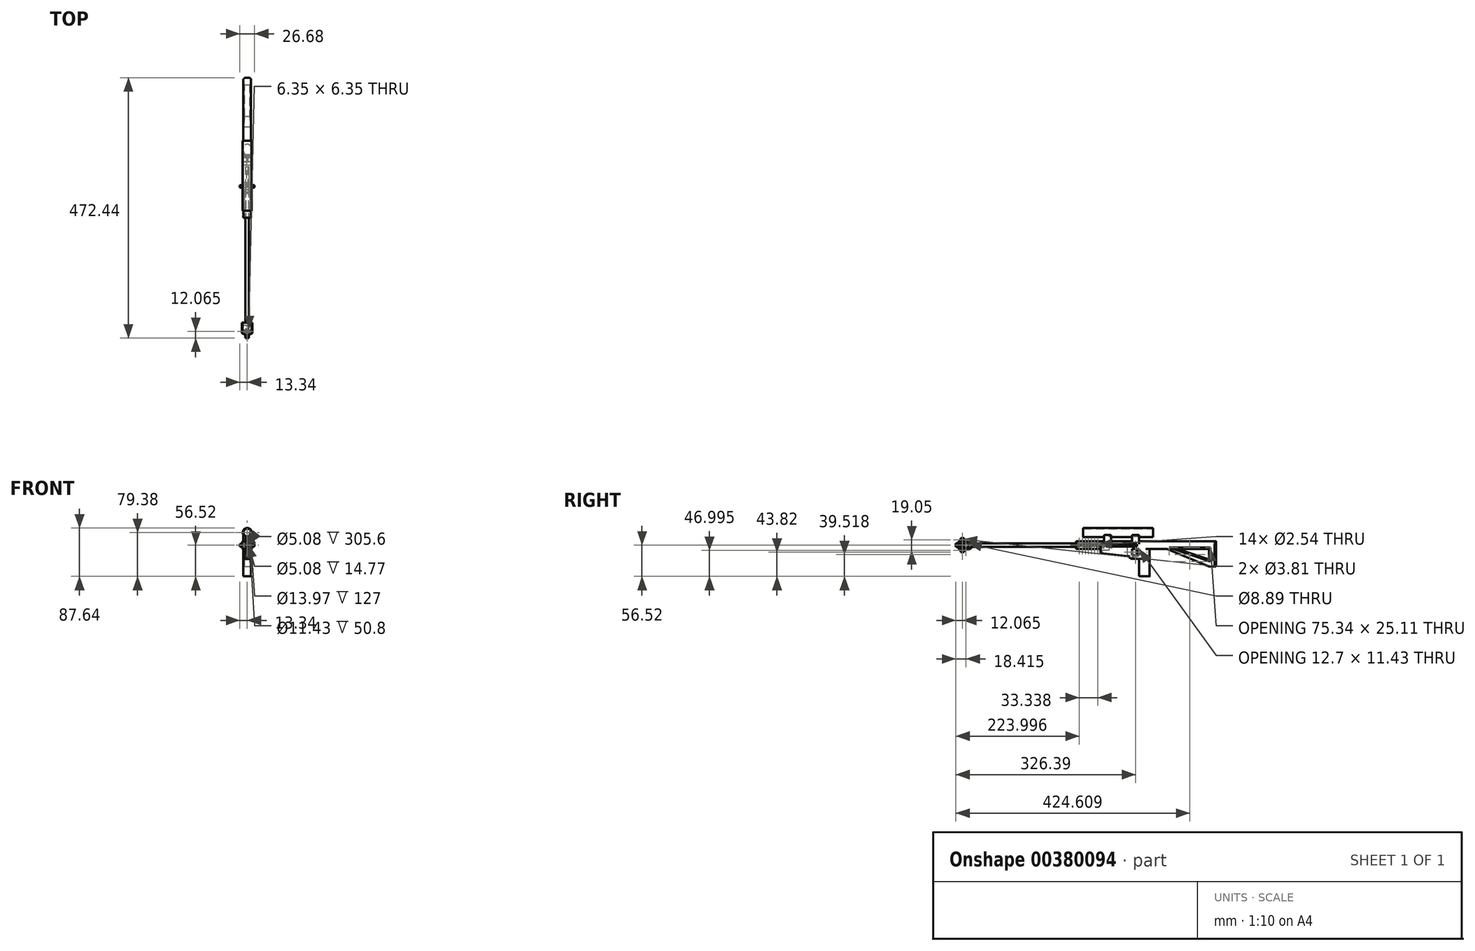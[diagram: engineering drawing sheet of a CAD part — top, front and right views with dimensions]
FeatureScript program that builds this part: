
annotation { "Feature Type Name" : "Feature", "Feature Type Description" : "" }
export const myFeature = defineFeature(function(context is Context, id is Id, definition is map)
    precondition{}
    {
        {
            var Q0;
            Q0=qCreatedBy(makeId("Front.planeOp"),FACE);
            var sketch = newSketch(context, id + "F0", { "sketchPlane" : qUnion([Q0])});
            skLineSegment(sketch, "E0.bottom", {"start": v(9.53, -6.35) * mm, "end": v(-9.53, -6.35) * mm});
            skLineSegment(sketch, "E0.top", {"start": v(9.53, 6.35) * mm, "end": v(-9.53, 6.35) * mm});
            skLineSegment(sketch, "E0.left", {"start": v(9.53, -6.35) * mm, "end": v(9.53, 6.35) * mm});
            skLineSegment(sketch, "E0.right", {"start": v(-9.53, -6.35) * mm, "end": v(-9.53, 6.35) * mm});
            skPoint(sketch, "E0.middle", {"position": v(0, 0) * mm});
            skSolve(sketch);
        }
        {
            var Q0;
            Q0=qSketchRegion(id+"F0",true);
            extrude(context, id + "F1", {"entities" : qUnion([Q0]), "depth" : 25.4 * mm});
        }
        {
            var Q0;
            Q0=makeQuery(id+"F1.opExtrude","CAP_FACE",FACE,{"disambiguationData":[OSD([sQuery(id+"F0.wireOp",EDGE,"E0.bottom"),sQuery(id+"F0.wireOp",EDGE,"E0.top"),sQuery(id+"F0.wireOp",EDGE,"E0.left"),sQuery(id+"F0.wireOp",EDGE,"E0.right")])],"isStart":true});
            var sketch = newSketch(context, id + "F2", { "sketchPlane" : qUnion([Q0])});
            skCircle(sketch, "E1", {"center": v(0, 0) * mm, "radius": 3.18 * mm});
            skSolve(sketch);
        }
        {
            var Q0;
            Q0=qSketchRegion(id+"F2",true);
            extrude(context, id + "F3", {"entities" : qUnion([Q0]), "operationType" : NewBodyOperationType.ADD, "depth" : 190.5 * mm});
        }
        {
            var Q0;
            Q0=qCreatedBy(makeId("Front.planeOp"),FACE);
            var sketch = newSketch(context, id + "F4", { "sketchPlane" : qUnion([Q0])});
            skLineSegment(sketch, "E2.bottom", {"start": v(3.17, -12.7) * mm, "end": v(-3.18, -12.7) * mm});
            skLineSegment(sketch, "E2.top", {"start": v(3.18, 12.7) * mm, "end": v(-3.17, 12.7) * mm});
            skLineSegment(sketch, "E2.left", {"start": v(3.17, -12.7) * mm, "end": v(3.18, 12.7) * mm});
            skLineSegment(sketch, "E2.right", {"start": v(-3.18, -12.7) * mm, "end": v(-3.17, 12.7) * mm});
            skPoint(sketch, "E2.middle", {"position": v(0, 0) * mm});
            skSolve(sketch);
        }
        {
            var Q0;
            Q0 = qSketchRegion(id + "F4", true);
            extrude(context, id + "F5", {"entities" : qUnion([Q0]), "operationType" : NewBodyOperationType.ADD, "depth" : 19.05 * mm, "hasSecondDirection" : true, "secondDirectionOppositeDirection" : true, "secondDirectionDepth" : -12.7 * mm});
        }
        {
            var Q0;
            Q0=makeQuery(id+"F3.opExtrude","CAP_FACE",FACE,{"disambiguationData":[OSD([sQuery(id+"F2.wireOp",EDGE,"E1")])],"isStart":false});
            var sketch = newSketch(context, id + "F6", { "sketchPlane" : qUnion([Q0])});
            skLineSegment(sketch, "E3.bottom", {"start": v(6.99, -6.99) * mm, "end": v(-6.99, -6.99) * mm});
            skLineSegment(sketch, "E3.top", {"start": v(6.98, 6.99) * mm, "end": v(-6.98, 6.99) * mm});
            skLineSegment(sketch, "E3.left", {"start": v(6.99, -6.99) * mm, "end": v(6.99, 6.98) * mm});
            skLineSegment(sketch, "E3.right", {"start": v(-6.99, -6.99) * mm, "end": v(-6.99, 6.98) * mm});
            skPoint(sketch, "E3.middle", {"position": v(0, 0) * mm});
            skSolve(sketch);
        }
        {
            var Q0;
            Q0=qSketchRegion(id+"F6",true);
            extrude(context, id + "F7", {"entities" : qUnion([Q0]), "operationType" : NewBodyOperationType.ADD, "depth" : 254 * mm});
        }
        {
            var Q0;
            Q0=makeQuery(id+"F7.opExtrude","SWEPT_FACE",FACE,{"disambiguationData":[OSD([sQuery(id+"F6.wireOp",EDGE,"E3.right")])]});
            var sketch = newSketch(context, id + "F8", { "sketchPlane" : qUnion([Q0])});
            skLineSegment(sketch, "E4", {"start": v(444.5, -6.99) * mm, "end": v(444.5, -38.74) * mm});
            skLineSegment(sketch, "E5", {"start": v(444.5, -38.74) * mm, "end": v(431.8, -38.74) * mm});
            skLineSegment(sketch, "E6", {"start": v(431.8, -38.74) * mm, "end": v(431.8, -6.99) * mm});
            skSolve(sketch);
        }
        {
            var Q0;
            Q0=qSketchRegion(id+"F8",true);
            var Q1;
            {var subQ0=sQuery(id+"F8.wireOp",EDGE,"E4");Q1=makeQuery(id+"F8.imprint","IMPRINT",FACE,{"disambiguationData":[TD([[makeQuery(id+"F8.imprint","IMPRINT",EDGE,{"derivedFrom":subQ0}),-1.0]])]});}
            extrude(context, id + "F9", {"entities" : qUnion([Q0, Q1]), "operationType" : NewBodyOperationType.ADD, "depth" : -13.97 * mm});
        }
        {
            var Q0;
            {var subQ0=sQuery(id+"F6.wireOp",EDGE,"E3.right");Q0=makeQuery(id+"F9.boolean.opBoolean","MERGE",FACE,{"derivedFrom":[makeQuery(id+"F7.opExtrude","SWEPT_FACE",FACE,{"disambiguationData":[OSD([subQ0])]}),makeQuery(id+"F9.opExtrude","CAP_FACE",FACE,{"disambiguationData":[OSD([sQuery(id+"F6.wireOp",EDGE,"E3.bottom"),subQ0,sQuery(id+"F8.wireOp",EDGE,"E4"),sQuery(id+"F8.wireOp",EDGE,"E5"),sQuery(id+"F8.wireOp",EDGE,"E6")])],"isStart":true})]});}
            var sketch = newSketch(context, id + "F10", { "sketchPlane" : qUnion([Q0])});
            skLineSegment(sketch, "E7", {"start": v(431.8, -38.74) * mm, "end": v(355.6, -6.98) * mm});
            skLineSegment(sketch, "E8", {"start": v(431.8, -38.74) * mm, "end": v(431.8, -26.04) * mm});
            skLineSegment(sketch, "E9", {"start": v(431.8, -26.03) * mm, "end": v(374.65, -6.98) * mm});
            skLineSegment(sketch, "E10", {"start": v(374.65, -6.99) * mm, "end": v(355.6, -6.99) * mm});
            skSolve(sketch);
        }
        {
            var Q0;
            Q0=qSketchRegion(id+"F10",true);
            extrude(context, id + "F11", {"entities" : qUnion([Q0]), "operationType" : NewBodyOperationType.ADD, "depth" : -13.97 * mm});
        }
        {
            var Q0;
            Q0=makeQuery(id+"F11.boolean.opBoolean","MERGE",FACE,{"derivedFrom":[makeQuery(id+"F9.boolean.opBoolean","MERGE",FACE,{"derivedFrom":[makeQuery(id+"F7.opExtrude","SWEPT_FACE",FACE,{"disambiguationData":[OSD([sQuery(id+"F6.wireOp",EDGE,"E3.left")])]}),makeQuery(id+"F9.opExtrude","CAP_FACE",FACE,{"disambiguationData":[OSD([sQuery(id+"F6.wireOp",EDGE,"E3.bottom"),sQuery(id+"F6.wireOp",EDGE,"E3.right"),sQuery(id+"F8.wireOp",EDGE,"E4"),sQuery(id+"F8.wireOp",EDGE,"E5"),sQuery(id+"F8.wireOp",EDGE,"E6")])],"isStart":false})]}),makeQuery(id+"F11.opExtrude","CAP_FACE",FACE,{"disambiguationData":[OSD([sQuery(id+"F10.wireOp",EDGE,"E7"),sQuery(id+"F10.wireOp",EDGE,"E8"),sQuery(id+"F10.wireOp",EDGE,"E9"),sQuery(id+"F10.wireOp",EDGE,"E10")])],"isStart":false})]});
            var sketch = newSketch(context, id + "F12", { "sketchPlane" : qUnion([Q0])});
            skLineSegment(sketch, "E11", {"start": v(-444.5, 6.98) * mm, "end": v(-190.5, 6.98) * mm});
            skLineSegment(sketch, "E12", {"start": v(-190.5, 6.98) * mm, "end": v(-317.5, 6.98) * mm});
            skLineSegment(sketch, "E13", {"start": v(-317.5, 6.98) * mm, "end": v(-317.5, -43.82) * mm});
            skLineSegment(sketch, "E14", {"start": v(-317.5, -43.82) * mm, "end": v(-304.8, -43.82) * mm});
            skLineSegment(sketch, "E15", {"start": v(-304.8, -43.82) * mm, "end": v(-304.8, 6.98) * mm});
            skLineSegment(sketch, "E16", {"start": v(-304.8, -18.42) * mm, "end": v(-292.1, -18.42) * mm});
            skLineSegment(sketch, "E17", {"start": v(-292.1, -18.42) * mm, "end": v(-292.1, -6.99) * mm});
            skLineSegment(sketch, "E18", {"start": v(-292.1, -6.99) * mm, "end": v(-285.75, -6.99) * mm});
            skLineSegment(sketch, "E19", {"start": v(-285.75, -6.99) * mm, "end": v(-285.75, -24.77) * mm});
            skLineSegment(sketch, "E20", {"start": v(-285.75, -24.77) * mm, "end": v(-304.8, -24.77) * mm});
            skLineSegment(sketch, "E21", {"start": v(-285.75, -6.99) * mm, "end": v(-280.67, -6.99) * mm});
            skLineSegment(sketch, "E22", {"start": v(-304.8, -43.82) * mm, "end": v(-304.8, -56.52) * mm});
            skLineSegment(sketch, "E23", {"start": v(-317.5, -43.82) * mm, "end": v(-317.5, -56.52) * mm});
            skLineSegment(sketch, "E24", {"start": v(-304.8, -56.52) * mm, "end": v(-317.5, -56.52) * mm});
            skLineSegment(sketch, "E25", {"start": v(-317.5, -56.52) * mm, "end": v(-323.85, -56.52) * mm});
            skLineSegment(sketch, "E26", {"start": v(-323.85, -56.52) * mm, "end": v(-323.85, -6.99) * mm});
            skSolve(sketch);
        }
        {
            var Q0;
            Q0=qSketchRegion(id+"F12",true);
            var Q1;
            {var subQ8=sQuery(id+"F12.wireOp",EDGE,"E23");Q1=makeQuery(id+"F12.imprint","IMPRINT",FACE,{"disambiguationData":[TD([[makeQuery(id+"F12.imprint","IMPRINT",EDGE,{"derivedFrom":subQ8}),-1.0]])]});}
            extrude(context, id + "F13", {"entities" : qUnion([Q0, Q1]), "operationType" : NewBodyOperationType.ADD, "depth" : -13.97 * mm});
        }
        {
            var Q0;
            Q0=makeQuery(id+"F13.opExtrude","SWEPT_EDGE",EDGE,{"disambiguationData":[OSD([sQuery(id+"F12.wireOp",EDGE,"E19"),sQuery(id+"F12.wireOp",EDGE,"E20")])]});
            fillet(context, id + "F14", {"entities" : qUnion([Q0]), "radius" : 6.35 * mm, "tangentPropagation" : true, "allowEdgeOverflow" : false});
        }
        {
            var Q0;
            Q0=makeQuery(id+"F13.boolean.opBoolean","MERGE",FACE,{"derivedFrom":[makeQuery(id+"F11.boolean.opBoolean","MERGE",FACE,{"derivedFrom":[makeQuery(id+"F9.boolean.opBoolean","MERGE",FACE,{"derivedFrom":[makeQuery(id+"F7.opExtrude","SWEPT_FACE",FACE,{"disambiguationData":[OSD([sQuery(id+"F6.wireOp",EDGE,"E3.left")])]}),makeQuery(id+"F9.opExtrude","CAP_FACE",FACE,{"disambiguationData":[OSD([sQuery(id+"F6.wireOp",EDGE,"E3.bottom"),sQuery(id+"F6.wireOp",EDGE,"E3.right"),sQuery(id+"F8.wireOp",EDGE,"E4"),sQuery(id+"F8.wireOp",EDGE,"E5"),sQuery(id+"F8.wireOp",EDGE,"E6")])],"isStart":false})]}),makeQuery(id+"F11.opExtrude","CAP_FACE",FACE,{"disambiguationData":[OSD([sQuery(id+"F10.wireOp",EDGE,"E7"),sQuery(id+"F10.wireOp",EDGE,"E8"),sQuery(id+"F10.wireOp",EDGE,"E9"),sQuery(id+"F10.wireOp",EDGE,"E10")])],"isStart":false})]}),makeQuery(id+"F13.opExtrude","CAP_FACE",FACE,{"disambiguationData":[OSD([sQuery(id+"F12.wireOp",EDGE,"E12"),sQuery(id+"F12.wireOp",EDGE,"E13"),sQuery(id+"F12.wireOp",EDGE,"E14"),sQuery(id+"F12.wireOp",EDGE,"E15"),sQuery(id+"F12.wireOp",EDGE,"E16"),sQuery(id+"F12.wireOp",EDGE,"E17"),sQuery(id+"F12.wireOp",EDGE,"E18"),sQuery(id+"F12.wireOp",EDGE,"E19"),sQuery(id+"F12.wireOp",EDGE,"E20")])],"isStart":true})]});
            var sketch = newSketch(context, id + "F15", { "sketchPlane" : qUnion([Q0])});
            skLineSegment(sketch, "E27", {"start": v(-234.95, -22.23) * mm, "end": v(-234.95, -6.99) * mm});
            skLineSegment(sketch, "E28", {"start": v(-234.95, -22.23) * mm, "end": v(-285.75, -22.23) * mm});
            skLineSegment(sketch, "E29", {"start": v(-285.75, -22.23) * mm, "end": v(-285.75, -6.99) * mm});
            skSolve(sketch);
        }
        {
            var Q0;
            Q0=qSketchRegion(id+"F15",true);
            var Q1;
            {var subQ0=sQuery(id+"F15.wireOp",EDGE,"gqdgmxWL-FIIV-5ZZU-RBbH-KmW0Z6Do0HDY");Q1=makeQuery(id+"F15.imprint","IMPRINT",FACE,{"disambiguationData":[TD([[makeQuery(id+"F15.imprint","IMPRINT",EDGE,{"derivedFrom":subQ0}),1.0]])]});}
            var Q2;
            {var subQ17=sQuery(id+"F15.wireOp",EDGE,"E27");Q2=makeQuery(id+"F15.imprint","IMPRINT",FACE,{"disambiguationData":[TD([[makeQuery(id+"F15.imprint","IMPRINT",EDGE,{"derivedFrom":subQ17}),1.0]])]});}
            extrude(context, id + "F16", {"entities" : qUnion([Q0, Q1, Q2]), "operationType" : NewBodyOperationType.ADD, "depth" : -13.97 * mm});
        }
        {
            var Q0;
            {var subQ0=sQuery(id+"F6.wireOp",EDGE,"E3.left");var subQ1=sQuery(id+"F6.wireOp",EDGE,"E3.bottom");Q0=makeQuery(id+"F16.boolean.opBoolean","MERGE",FACE,{"derivedFrom":[makeQuery(id+"F13.boolean.opBoolean","MERGE",FACE,{"derivedFrom":[makeQuery(id+"F11.boolean.opBoolean","MERGE",FACE,{"derivedFrom":[makeQuery(id+"F9.boolean.opBoolean","MERGE",FACE,{"derivedFrom":[makeQuery(id+"F7.opExtrude","SWEPT_FACE",FACE,{"disambiguationData":[OSD([subQ0])]}),makeQuery(id+"F9.opExtrude","CAP_FACE",FACE,{"disambiguationData":[OSD([subQ1,sQuery(id+"F6.wireOp",EDGE,"E3.right"),sQuery(id+"F8.wireOp",EDGE,"E4"),sQuery(id+"F8.wireOp",EDGE,"E5"),sQuery(id+"F8.wireOp",EDGE,"E6")])],"isStart":false})]}),makeQuery(id+"F11.opExtrude","CAP_FACE",FACE,{"disambiguationData":[OSD([sQuery(id+"F10.wireOp",EDGE,"E7"),sQuery(id+"F10.wireOp",EDGE,"E8"),sQuery(id+"F10.wireOp",EDGE,"E9"),sQuery(id+"F10.wireOp",EDGE,"E10")])],"isStart":false})]}),makeQuery(id+"F13.opExtrude","CAP_FACE",FACE,{"disambiguationData":[OSD([sQuery(id+"F12.wireOp",EDGE,"E12"),sQuery(id+"F12.wireOp",EDGE,"E13"),sQuery(id+"F12.wireOp",EDGE,"E14"),sQuery(id+"F12.wireOp",EDGE,"E15"),sQuery(id+"F12.wireOp",EDGE,"E16"),sQuery(id+"F12.wireOp",EDGE,"E17"),sQuery(id+"F12.wireOp",EDGE,"E18"),sQuery(id+"F12.wireOp",EDGE,"E19"),sQuery(id+"F12.wireOp",EDGE,"E20")])],"isStart":true})]}),makeQuery(id+"F16.opExtrude","CAP_FACE",FACE,{"disambiguationData":[OSD([subQ1,subQ0,sQuery(id+"F15.wireOp",EDGE,"gqdgmxWL-FIIV-5ZZU-RBbH-KmW0Z6Do0HDY"),sQuery(id+"F15.wireOp",EDGE,"u0oC4iEc-4FHG-jWvm-i2Hm-SS8I0tg0rfsX"),sQuery(id+"F15.wireOp",EDGE,"E27")])],"isStart":true})]});}
            var sketch = newSketch(context, id + "F17", { "sketchPlane" : qUnion([Q0])});
            skLineSegment(sketch, "E30", {"start": v(-304.8, -6.99) * mm, "end": v(-304.8, 18.41) * mm});
            skLineSegment(sketch, "E31", {"start": v(-292.1, -6.99) * mm, "end": v(-292.1, 18.41) * mm});
            skLineSegment(sketch, "E32", {"start": v(-304.8, 18.41) * mm, "end": v(-292.1, 18.41) * mm});
            skLineSegment(sketch, "E33", {"start": v(-292.1, -6.99) * mm, "end": v(-254, -6.99) * mm});
            skLineSegment(sketch, "E34", {"start": v(-254, -6.99) * mm, "end": v(-254, 18.41) * mm});
            skLineSegment(sketch, "E35", {"start": v(-254, 18.41) * mm, "end": v(-241.3, 18.41) * mm});
            skLineSegment(sketch, "E36", {"start": v(-241.3, 18.41) * mm, "end": v(-241.3, 6.98) * mm});
            skSolve(sketch);
        }
        {
            var Q0;
            Q0=qSketchRegion(id+"F17",true);
            var Q1;
            {var subQ0=sQuery(id+"F17.wireOp",EDGE,"E32");Q1=makeQuery(id+"F17.imprint","IMPRINT",FACE,{"disambiguationData":[TD([[makeQuery(id+"F17.imprint","IMPRINT",EDGE,{"derivedFrom":subQ0}),-1.0]])]});}
            var Q2;
            {var subQ0=sQuery(id+"F17.wireOp",EDGE,"E35");Q2=makeQuery(id+"F17.imprint","IMPRINT",FACE,{"disambiguationData":[TD([[makeQuery(id+"F17.imprint","IMPRINT",EDGE,{"derivedFrom":subQ0}),-1.0]])]});}
            extrude(context, id + "F18", {"entities" : qUnion([Q0, Q1, Q2]), "operationType" : NewBodyOperationType.ADD, "depth" : -13.97 * mm});
        }
        {
            var Q0;
            Q0=makeQuery(id+"F18.opExtrude","SWEPT_FACE",FACE,{"disambiguationData":[OSD([sQuery(id+"F17.wireOp",EDGE,"E30")])]});
            var sketch = newSketch(context, id + "F19", { "sketchPlane" : qUnion([Q0])});
            skLineSegment(sketch, "E37", {"start": v(0, 0) * mm, "end": v(0, 22.86) * mm});
            skPoint(sketch, "E37.endSnap0", {"position": v(0, 18.41) * mm});
            skCircle(sketch, "E38", {"center": v(0, 22.86) * mm, "radius": 8.26 * mm});
            skSolve(sketch);
        }
        {
            var Q0;
            Q0=qSketchRegion(id+"F19",true);
            extrude(context, id + "F20", {"entities" : qUnion([Q0]), "operationType" : NewBodyOperationType.ADD, "depth" : 25.4 * mm, "hasSecondDirection" : true, "secondDirectionOppositeDirection" : true, "secondDirectionDepth" : 101.6 * mm});
        }
        {
            var Q0;
            Q0=makeQuery(id+"F16.opExtrude","SWEPT_FACE",FACE,{"disambiguationData":[OSD([sQuery(id+"F15.wireOp",EDGE,"E28")])]});
            var sketch = newSketch(context, id + "F21", { "sketchPlane" : qUnion([Q0])});
            skLineSegment(sketch, "E39", {"start": v(-3.5, -283.21) * mm, "end": v(3.5, -283.21) * mm});
            skLineSegment(sketch, "E40", {"start": v(-3.5, -237.49) * mm, "end": v(3.5, -237.49) * mm});
            skLineSegment(sketch, "E41", {"start": v(-3.5, -283.21) * mm, "end": v(-3.5, -237.49) * mm});
            skLineSegment(sketch, "E42", {"start": v(3.5, -237.49) * mm, "end": v(3.5, -283.21) * mm});
            skLineSegment(sketch, "E43", {"start": v(3.5, -283.21) * mm, "end": v(3.5, -237.49) * mm});
            skLineSegment(sketch, "E44", {"start": v(3.5, -237.49) * mm, "end": v(-3.5, -237.49) * mm});
            skLineSegment(sketch, "E45", {"start": v(-3.5, -237.49) * mm, "end": v(-3.5, -283.21) * mm});
            skSolve(sketch);
        }
        {
            var Q0;
            Q0=qSketchRegion(id+"F21",true);
            extrude(context, id + "F22", {"entities" : qUnion([Q0]), "operationType" : NewBodyOperationType.REMOVE, "oppositeDirection" : true, "depth" : 12.7 * mm});
        }
        {
            var Q0;
            Q0=makeQuery(id+"F16.opExtrude","SWEPT_EDGE",EDGE,{"disambiguationData":[OSD([sQuery(id+"F15.wireOp",EDGE,"E27"),sQuery(id+"F15.wireOp",EDGE,"E28")])]});
            chamfer(context, id + "F23", {"entities" : qUnion([Q0]), "chamferType" : ChamferType.OFFSET_ANGLE, "width" : 7.62 * mm, "oppositeDirection" : true, "angle" : 84 * degree, "tangentPropagation" : true});
        }
        {
            var Q0;
            Q0=makeQuery(id+"F9.boolean.opBoolean","MERGE",EDGE,{"derivedFrom":[makeQuery(id+"F7.opExtrude","CAP_EDGE",EDGE,{"disambiguationData":[OSD([sQuery(id+"F6.wireOp",EDGE,"E3.left")])],"isStart":false}),makeQuery(id+"F9.opExtrude","CAP_EDGE",EDGE,{"disambiguationData":[OSD([sQuery(id+"F8.wireOp",EDGE,"E4")])],"isStart":false})]});
            var Q1;
            Q1=makeQuery(id+"F9.boolean.opBoolean","MERGE",EDGE,{"derivedFrom":[makeQuery(id+"F7.opExtrude","CAP_EDGE",EDGE,{"disambiguationData":[OSD([sQuery(id+"F6.wireOp",EDGE,"E3.right")])],"isStart":false}),makeQuery(id+"F9.opExtrude","CAP_EDGE",EDGE,{"disambiguationData":[OSD([sQuery(id+"F8.wireOp",EDGE,"E4")])],"isStart":true})]});
            chamfer(context, id + "F24", {"entities" : qUnion([Q0, Q1]), "width" : 2.54 * mm, "tangentPropagation" : true});
        }
        {
            var Q0;
            {var subQ1=sQuery(id+"F6.wireOp",EDGE,"E3.left");var subQ2=sQuery(id+"F6.wireOp",EDGE,"E3.top");var subQ3=sQuery(id+"F8.wireOp",EDGE,"E4");Q0=makeQuery(id+"F18.boolean.opBoolean","SPLIT",EDGE,{"disambiguationData":[TD([makeQuery(id+"F9.opExtrude","SWEPT_FACE",FACE,{"disambiguationData":[OSD([subQ3])]})])],"derivedFrom":makeQuery(id+"F7.opExtrude","SWEPT_EDGE",EDGE,{"disambiguationData":[OSD([subQ2,subQ1])]})});}
            var Q1;
            {var subQ2=sQuery(id+"F6.wireOp",EDGE,"E3.top");var subQ3=sQuery(id+"F6.wireOp",EDGE,"E3.right");var subQ5=sQuery(id+"F8.wireOp",EDGE,"E4");Q1=makeQuery(id+"F18.boolean.opBoolean","SPLIT",EDGE,{"disambiguationData":[TD([makeQuery(id+"F9.opExtrude","SWEPT_FACE",FACE,{"disambiguationData":[OSD([subQ5])]})])],"derivedFrom":makeQuery(id+"F7.opExtrude","SWEPT_EDGE",EDGE,{"disambiguationData":[OSD([subQ2,subQ3])]})});}
            var Q2;
            {var subQ2=sQuery(id+"F6.wireOp",EDGE,"E3.left");var subQ3=sQuery(id+"F6.wireOp",EDGE,"E3.top");var subQ4=sQuery(id+"F17.wireOp",EDGE,"E31");Q2=makeQuery(id+"F18.boolean.opBoolean","SPLIT",EDGE,{"disambiguationData":[TD([makeQuery(id+"F18.opExtrude","SWEPT_FACE",FACE,{"disambiguationData":[OSD([subQ4])]})])],"derivedFrom":makeQuery(id+"F7.opExtrude","SWEPT_EDGE",EDGE,{"disambiguationData":[OSD([subQ3,subQ2])]})});}
            var Q3;
            {var subQ0=sQuery(id+"F6.wireOp",EDGE,"E3.right");var subQ2=sQuery(id+"F6.wireOp",EDGE,"E3.top");var subQ5=sQuery(id+"F17.wireOp",EDGE,"E31");Q3=makeQuery(id+"F18.boolean.opBoolean","SPLIT",EDGE,{"disambiguationData":[TD([makeQuery(id+"F18.opExtrude","SWEPT_FACE",FACE,{"disambiguationData":[OSD([subQ5])]})])],"derivedFrom":makeQuery(id+"F7.opExtrude","SWEPT_EDGE",EDGE,{"disambiguationData":[OSD([subQ2,subQ0])]})});}
            fillet(context, id + "F25", {"entities" : qUnion([Q0, Q1, Q2, Q3]), "radius" : 5.08 * mm, "tangentPropagation" : true, "allowEdgeOverflow" : false});
        }
        {
            var Q0;
            Q0=makeQuery(id+"F1.opExtrude","CAP_EDGE",EDGE,{"disambiguationData":[OSD([sQuery(id+"F0.wireOp",EDGE,"E0.left")])],"isStart":false});
            var Q1;
            Q1=makeQuery(id+"F1.opExtrude","CAP_EDGE",EDGE,{"disambiguationData":[OSD([sQuery(id+"F0.wireOp",EDGE,"E0.right")])],"isStart":false});
            chamfer(context, id + "F26", {"entities" : qUnion([Q0, Q1]), "chamferType" : ChamferType.OFFSET_ANGLE, "width" : 6.35 * mm, "oppositeDirection" : true, "angle" : 64 * degree, "tangentPropagation" : true});
        }
        {
            var Q0;
            Q0=qCreatedBy(makeId("Front.planeOp"),FACE);
            var sketch = newSketch(context, id + "F27", { "sketchPlane" : qUnion([Q0])});
            skCircle(sketch, "E46", {"center": v(0, 0) * mm, "radius": 3.18 * mm});
            skSolve(sketch);
        }
        {
            var Q0;
            Q0=qSketchRegion(id+"F27",true);
            extrude(context, id + "F28", {"entities" : qUnion([Q0]), "operationType" : NewBodyOperationType.ADD, "depth" : 27.94 * mm});
        }
        {
            var Q0;
            Q0=makeQuery(id+"F1.opExtrude","SWEPT_FACE",FACE,{"disambiguationData":[OSD([sQuery(id+"F0.wireOp",EDGE,"E0.right")])]});
            var sketch = newSketch(context, id + "F29", { "sketchPlane" : qUnion([Q0])});
            skLineSegment(sketch, "E47", {"start": v(0, 0) * mm, "end": v(19.05, 0) * mm});
            skLineSegment(sketch, "E48", {"start": v(19.05, 0) * mm, "end": v(9.53, 0) * mm});
            skCircle(sketch, "E49", {"center": v(9.53, 0) * mm, "radius": 4.45 * mm});
            skSolve(sketch);
        }
        {
            var Q0;
            Q0=qSketchRegion(id+"F29",true);
            extrude(context, id + "F30", {"entities" : qUnion([Q0]), "operationType" : NewBodyOperationType.REMOVE, "oppositeDirection" : true, "depth" : 50.8 * mm});
        }
        {
            var Q0;
            Q0=makeQuery(id+"F28.opExtrude","CAP_FACE",FACE,{"disambiguationData":[OSD([sQuery(id+"F27.wireOp",EDGE,"E46")])],"isStart":false});
            var sketch = newSketch(context, id + "F31", { "sketchPlane" : qUnion([Q0])});
            skCircle(sketch, "E50", {"center": v(0, 0) * mm, "radius": 2.54 * mm});
            skSolve(sketch);
        }
        {
            var Q0;
            Q0=qSketchRegion(id+"F31",true);
            extrude(context, id + "F32", {"entities" : qUnion([Q0]), "operationType" : NewBodyOperationType.REMOVE, "oppositeDirection" : true, "depth" : 327.66 * mm});
        }
        {
            var Q0;
            {var subQ0=sQuery(id+"F6.wireOp",EDGE,"E3.left");var subQ1=sQuery(id+"F6.wireOp",EDGE,"E3.top");var subQ2=sQuery(id+"F6.wireOp",EDGE,"E3.bottom");Q0=makeQuery(id+"F18.boolean.opBoolean","MERGE",FACE,{"derivedFrom":[makeQuery(id+"F16.boolean.opBoolean","MERGE",FACE,{"derivedFrom":[makeQuery(id+"F13.boolean.opBoolean","MERGE",FACE,{"derivedFrom":[makeQuery(id+"F11.boolean.opBoolean","MERGE",FACE,{"derivedFrom":[makeQuery(id+"F9.boolean.opBoolean","MERGE",FACE,{"derivedFrom":[makeQuery(id+"F7.opExtrude","SWEPT_FACE",FACE,{"disambiguationData":[OSD([subQ0])]}),makeQuery(id+"F9.opExtrude","CAP_FACE",FACE,{"disambiguationData":[OSD([subQ2,sQuery(id+"F6.wireOp",EDGE,"E3.right"),sQuery(id+"F8.wireOp",EDGE,"E4"),sQuery(id+"F8.wireOp",EDGE,"E5"),sQuery(id+"F8.wireOp",EDGE,"E6")])],"isStart":false})]}),makeQuery(id+"F11.opExtrude","CAP_FACE",FACE,{"disambiguationData":[OSD([sQuery(id+"F10.wireOp",EDGE,"E7"),sQuery(id+"F10.wireOp",EDGE,"E8"),sQuery(id+"F10.wireOp",EDGE,"E9"),sQuery(id+"F10.wireOp",EDGE,"E10")])],"isStart":false})]}),makeQuery(id+"F13.opExtrude","CAP_FACE",FACE,{"disambiguationData":[OSD([sQuery(id+"F12.wireOp",EDGE,"E12"),sQuery(id+"F12.wireOp",EDGE,"E13"),sQuery(id+"F12.wireOp",EDGE,"E14"),sQuery(id+"F12.wireOp",EDGE,"E15"),sQuery(id+"F12.wireOp",EDGE,"E16"),sQuery(id+"F12.wireOp",EDGE,"E17"),sQuery(id+"F12.wireOp",EDGE,"E18"),sQuery(id+"F12.wireOp",EDGE,"E19"),sQuery(id+"F12.wireOp",EDGE,"E20")])],"isStart":true})]}),makeQuery(id+"F16.opExtrude","CAP_FACE",FACE,{"disambiguationData":[OSD([subQ2,subQ0,sQuery(id+"F15.wireOp",EDGE,"E27"),sQuery(id+"F15.wireOp",EDGE,"E28"),sQuery(id+"F15.wireOp",EDGE,"E29")])],"isStart":true})]}),makeQuery(id+"F18.opExtrude","CAP_FACE",FACE,{"disambiguationData":[OSD([subQ1,subQ0,sQuery(id+"F17.wireOp",EDGE,"E30"),sQuery(id+"F17.wireOp",EDGE,"E31"),sQuery(id+"F17.wireOp",EDGE,"E32")])],"isStart":true}),makeQuery(id+"F18.opExtrude","CAP_FACE",FACE,{"disambiguationData":[OSD([subQ1,subQ0,sQuery(id+"F17.wireOp",EDGE,"E34"),sQuery(id+"F17.wireOp",EDGE,"E35"),sQuery(id+"F17.wireOp",EDGE,"E36")])],"isStart":true})]});}
            var sketch = newSketch(context, id + "F33", { "sketchPlane" : qUnion([Q0])});
            skLineSegment(sketch, "E51", {"start": v(-300.99, 1.9) * mm, "end": v(-300.99, -2.54) * mm});
            skLineSegment(sketch, "E52", {"start": v(-300.99, -2.54) * mm, "end": v(-245.1, -2.54) * mm});
            skLineSegment(sketch, "E53", {"start": v(-300.99, 1.9) * mm, "end": v(-245.1, 1.9) * mm});
            skLineSegment(sketch, "E54", {"start": v(-245.1, 1.9) * mm, "end": v(-245.1, -2.54) * mm});
            skSolve(sketch);
        }
        {
            var Q0;
            Q0=qSketchRegion(id+"F33",true);
            extrude(context, id + "F34", {"entities" : qUnion([Q0]), "operationType" : NewBodyOperationType.REMOVE, "oppositeDirection" : true, "depth" : 25.4 * mm});
        }
        {
            var Q0;
            {var subQ0=sQuery(id+"F6.wireOp",EDGE,"E3.left");var subQ1=sQuery(id+"F6.wireOp",EDGE,"E3.top");var subQ2=sQuery(id+"F6.wireOp",EDGE,"E3.bottom");Q0=makeQuery(id+"F18.boolean.opBoolean","MERGE",FACE,{"derivedFrom":[makeQuery(id+"F16.boolean.opBoolean","MERGE",FACE,{"derivedFrom":[makeQuery(id+"F13.boolean.opBoolean","MERGE",FACE,{"derivedFrom":[makeQuery(id+"F11.boolean.opBoolean","MERGE",FACE,{"derivedFrom":[makeQuery(id+"F9.boolean.opBoolean","MERGE",FACE,{"derivedFrom":[makeQuery(id+"F7.opExtrude","SWEPT_FACE",FACE,{"disambiguationData":[OSD([subQ0])]}),makeQuery(id+"F9.opExtrude","CAP_FACE",FACE,{"disambiguationData":[OSD([subQ2,sQuery(id+"F6.wireOp",EDGE,"E3.right"),sQuery(id+"F8.wireOp",EDGE,"E4"),sQuery(id+"F8.wireOp",EDGE,"E5"),sQuery(id+"F8.wireOp",EDGE,"E6")])],"isStart":false})]}),makeQuery(id+"F11.opExtrude","CAP_FACE",FACE,{"disambiguationData":[OSD([sQuery(id+"F10.wireOp",EDGE,"E7"),sQuery(id+"F10.wireOp",EDGE,"E8"),sQuery(id+"F10.wireOp",EDGE,"E9"),sQuery(id+"F10.wireOp",EDGE,"E10")])],"isStart":false})]}),makeQuery(id+"F13.opExtrude","CAP_FACE",FACE,{"disambiguationData":[OSD([sQuery(id+"F12.wireOp",EDGE,"E12"),sQuery(id+"F12.wireOp",EDGE,"E13"),sQuery(id+"F12.wireOp",EDGE,"E14"),sQuery(id+"F12.wireOp",EDGE,"E15"),sQuery(id+"F12.wireOp",EDGE,"E16"),sQuery(id+"F12.wireOp",EDGE,"E17"),sQuery(id+"F12.wireOp",EDGE,"E18"),sQuery(id+"F12.wireOp",EDGE,"E19"),sQuery(id+"F12.wireOp",EDGE,"E20")])],"isStart":true})]}),makeQuery(id+"F16.opExtrude","CAP_FACE",FACE,{"disambiguationData":[OSD([subQ2,subQ0,sQuery(id+"F15.wireOp",EDGE,"E27"),sQuery(id+"F15.wireOp",EDGE,"E28"),sQuery(id+"F15.wireOp",EDGE,"E29")])],"isStart":true})]}),makeQuery(id+"F18.opExtrude","CAP_FACE",FACE,{"disambiguationData":[OSD([subQ1,subQ0,sQuery(id+"F17.wireOp",EDGE,"E30"),sQuery(id+"F17.wireOp",EDGE,"E31"),sQuery(id+"F17.wireOp",EDGE,"E32")])],"isStart":true}),makeQuery(id+"F18.opExtrude","CAP_FACE",FACE,{"disambiguationData":[OSD([subQ1,subQ0,sQuery(id+"F17.wireOp",EDGE,"E34"),sQuery(id+"F17.wireOp",EDGE,"E35"),sQuery(id+"F17.wireOp",EDGE,"E36")])],"isStart":true})]});}
            var sketch = newSketch(context, id + "F35", { "sketchPlane" : qUnion([Q0])});
            skLineSegment(sketch, "E55", {"start": v(-245.1, -0.32) * mm, "end": v(-247.4, -0.32) * mm});
            skCircle(sketch, "E56", {"center": v(-247.4, -0.32) * mm, "radius": 2.16 * mm});
            skLineSegment(sketch, "E57", {"start": v(-247.4, -1.33) * mm, "end": v(-247.4, -0.32) * mm});
            skLineSegment(sketch, "E58", {"start": v(-247.4, -0.32) * mm, "end": v(-247.4, 0.7) * mm});
            skLineSegment(sketch, "E59", {"start": v(-247.4, 0.7) * mm, "end": v(-245.1, 0.7) * mm});
            skLineSegment(sketch, "E60", {"start": v(-247.4, -1.33) * mm, "end": v(-245.1, -1.33) * mm});
            skLineSegment(sketch, "E61", {"start": v(-245.1, -1.33) * mm, "end": v(-245.1, -0.32) * mm});
            skLineSegment(sketch, "E62", {"start": v(-245.1, 0.7) * mm, "end": v(-245.1, -0.32) * mm});
            skSolve(sketch);
        }
        {
            var Q0;
            Q0=qSketchRegion(id+"F35",true);
            extrude(context, id + "F36", {"entities" : qUnion([Q0]), "operationType" : NewBodyOperationType.ADD, "depth" : -13.97 * mm});
        }
        {
            var Q0;
            {var subQ0=sQuery(id+"F6.wireOp",EDGE,"E3.left");var subQ1=sQuery(id+"F6.wireOp",EDGE,"E3.top");var subQ2=sQuery(id+"F6.wireOp",EDGE,"E3.bottom");var subQ3=sQuery(id+"F6.wireOp",EDGE,"E3.right");Q0=makeQuery(id+"F36.boolean.opBoolean","MERGE",FACE,{"derivedFrom":[makeQuery(id+"F18.boolean.opBoolean","MERGE",FACE,{"derivedFrom":[makeQuery(id+"F16.boolean.opBoolean","MERGE",FACE,{"derivedFrom":[makeQuery(id+"F13.boolean.opBoolean","MERGE",FACE,{"derivedFrom":[makeQuery(id+"F11.boolean.opBoolean","MERGE",FACE,{"derivedFrom":[makeQuery(id+"F9.boolean.opBoolean","MERGE",FACE,{"derivedFrom":[makeQuery(id+"F7.opExtrude","SWEPT_FACE",FACE,{"disambiguationData":[OSD([subQ3])]}),makeQuery(id+"F9.opExtrude","CAP_FACE",FACE,{"disambiguationData":[OSD([subQ2,subQ3,sQuery(id+"F8.wireOp",EDGE,"E4"),sQuery(id+"F8.wireOp",EDGE,"E5"),sQuery(id+"F8.wireOp",EDGE,"E6")])],"isStart":true})]}),makeQuery(id+"F11.opExtrude","CAP_FACE",FACE,{"disambiguationData":[OSD([sQuery(id+"F10.wireOp",EDGE,"E7"),sQuery(id+"F10.wireOp",EDGE,"E8"),sQuery(id+"F10.wireOp",EDGE,"E9"),sQuery(id+"F10.wireOp",EDGE,"E10")])],"isStart":true})]}),makeQuery(id+"F13.opExtrude","CAP_FACE",FACE,{"disambiguationData":[OSD([sQuery(id+"F12.wireOp",EDGE,"E12"),sQuery(id+"F12.wireOp",EDGE,"E13"),sQuery(id+"F12.wireOp",EDGE,"E14"),sQuery(id+"F12.wireOp",EDGE,"E15"),sQuery(id+"F12.wireOp",EDGE,"E16"),sQuery(id+"F12.wireOp",EDGE,"E17"),sQuery(id+"F12.wireOp",EDGE,"E18"),sQuery(id+"F12.wireOp",EDGE,"E19"),sQuery(id+"F12.wireOp",EDGE,"E20")])],"isStart":false})]}),makeQuery(id+"F16.opExtrude","CAP_FACE",FACE,{"disambiguationData":[OSD([subQ2,subQ0,sQuery(id+"F15.wireOp",EDGE,"E27"),sQuery(id+"F15.wireOp",EDGE,"E28"),sQuery(id+"F15.wireOp",EDGE,"E29")])],"isStart":false})]}),makeQuery(id+"F18.opExtrude","CAP_FACE",FACE,{"disambiguationData":[OSD([subQ1,subQ0,sQuery(id+"F17.wireOp",EDGE,"E30"),sQuery(id+"F17.wireOp",EDGE,"E31"),sQuery(id+"F17.wireOp",EDGE,"E32")])],"isStart":false}),makeQuery(id+"F18.opExtrude","CAP_FACE",FACE,{"disambiguationData":[OSD([subQ1,subQ0,sQuery(id+"F17.wireOp",EDGE,"E34"),sQuery(id+"F17.wireOp",EDGE,"E35"),sQuery(id+"F17.wireOp",EDGE,"E36")])],"isStart":false})]}),makeQuery(id+"F36.opExtrude","CAP_FACE",FACE,{"disambiguationData":[OSD([sQuery(id+"F35.wireOp",EDGE,"E56"),sQuery(id+"F35.wireOp",EDGE,"E59"),sQuery(id+"F35.wireOp",EDGE,"E60"),sQuery(id+"F35.wireOp",EDGE,"E61"),sQuery(id+"F35.wireOp",EDGE,"E62")])],"isStart":false})]});}
            var sketch = newSketch(context, id + "F37", { "sketchPlane" : qUnion([Q0])});
            skCircle(sketch, "E63", {"center": v(247.4, -0.32) * mm, "radius": 2.16 * mm});
            skSolve(sketch);
        }
        {
            var Q0;
            Q0=qSketchRegion(id+"F37",true);
            extrude(context, id + "F38", {"entities" : qUnion([Q0]), "operationType" : NewBodyOperationType.ADD, "depth" : 6.35 * mm});
        }
        {
            var Q0;
            Q0=makeQuery(id+"F13.opExtrude","CAP_EDGE",EDGE,{"disambiguationData":[OSD([sQuery(id+"F12.wireOp",EDGE,"E26")])],"isStart":true});
            var Q1;
            Q1=makeQuery(id+"F13.opExtrude","CAP_EDGE",EDGE,{"disambiguationData":[OSD([sQuery(id+"F12.wireOp",EDGE,"E15"),sQuery(id+"F12.wireOp",EDGE,"E22")])],"isStart":true});
            var Q2;
            Q2=makeQuery(id+"F13.opExtrude","CAP_EDGE",EDGE,{"disambiguationData":[OSD([sQuery(id+"F12.wireOp",EDGE,"E15"),sQuery(id+"F12.wireOp",EDGE,"E22")])],"isStart":false});
            var Q3;
            Q3=makeQuery(id+"F13.opExtrude","CAP_EDGE",EDGE,{"disambiguationData":[OSD([sQuery(id+"F12.wireOp",EDGE,"E26")])],"isStart":false});
            fillet(context, id + "F39", {"entities" : qUnion([Q0, Q1, Q2, Q3]), "radius" : 7 * mm, "tangentPropagation" : true, "allowEdgeOverflow" : false});
        }
        {
            var Q0;
            {var subQ0=sQuery(id+"F6.wireOp",EDGE,"E3.left");var subQ1=sQuery(id+"F6.wireOp",EDGE,"E3.top");var subQ2=sQuery(id+"F6.wireOp",EDGE,"E3.bottom");Q0=makeQuery(id+"F36.boolean.opBoolean","MERGE",FACE,{"derivedFrom":[makeQuery(id+"F18.boolean.opBoolean","MERGE",FACE,{"derivedFrom":[makeQuery(id+"F16.boolean.opBoolean","MERGE",FACE,{"derivedFrom":[makeQuery(id+"F13.boolean.opBoolean","MERGE",FACE,{"derivedFrom":[makeQuery(id+"F11.boolean.opBoolean","MERGE",FACE,{"derivedFrom":[makeQuery(id+"F9.boolean.opBoolean","MERGE",FACE,{"derivedFrom":[makeQuery(id+"F7.opExtrude","SWEPT_FACE",FACE,{"disambiguationData":[OSD([subQ0])]}),makeQuery(id+"F9.opExtrude","CAP_FACE",FACE,{"disambiguationData":[OSD([subQ2,sQuery(id+"F6.wireOp",EDGE,"E3.right"),sQuery(id+"F8.wireOp",EDGE,"E4"),sQuery(id+"F8.wireOp",EDGE,"E5"),sQuery(id+"F8.wireOp",EDGE,"E6")])],"isStart":false})]}),makeQuery(id+"F11.opExtrude","CAP_FACE",FACE,{"disambiguationData":[OSD([sQuery(id+"F10.wireOp",EDGE,"E7"),sQuery(id+"F10.wireOp",EDGE,"E8"),sQuery(id+"F10.wireOp",EDGE,"E9"),sQuery(id+"F10.wireOp",EDGE,"E10")])],"isStart":false})]}),makeQuery(id+"F13.opExtrude","CAP_FACE",FACE,{"disambiguationData":[OSD([sQuery(id+"F12.wireOp",EDGE,"E12"),sQuery(id+"F12.wireOp",EDGE,"E13"),sQuery(id+"F12.wireOp",EDGE,"E14"),sQuery(id+"F12.wireOp",EDGE,"E15"),sQuery(id+"F12.wireOp",EDGE,"E16"),sQuery(id+"F12.wireOp",EDGE,"E17"),sQuery(id+"F12.wireOp",EDGE,"E18"),sQuery(id+"F12.wireOp",EDGE,"E19"),sQuery(id+"F12.wireOp",EDGE,"E20")])],"isStart":true})]}),makeQuery(id+"F16.opExtrude","CAP_FACE",FACE,{"disambiguationData":[OSD([subQ2,subQ0,sQuery(id+"F15.wireOp",EDGE,"E27"),sQuery(id+"F15.wireOp",EDGE,"E28"),sQuery(id+"F15.wireOp",EDGE,"E29")])],"isStart":true})]}),makeQuery(id+"F18.opExtrude","CAP_FACE",FACE,{"disambiguationData":[OSD([subQ1,subQ0,sQuery(id+"F17.wireOp",EDGE,"E30"),sQuery(id+"F17.wireOp",EDGE,"E31"),sQuery(id+"F17.wireOp",EDGE,"E32")])],"isStart":true}),makeQuery(id+"F18.opExtrude","CAP_FACE",FACE,{"disambiguationData":[OSD([subQ1,subQ0,sQuery(id+"F17.wireOp",EDGE,"E34"),sQuery(id+"F17.wireOp",EDGE,"E35"),sQuery(id+"F17.wireOp",EDGE,"E36")])],"isStart":true})]}),makeQuery(id+"F36.opExtrude","CAP_FACE",FACE,{"disambiguationData":[OSD([sQuery(id+"F35.wireOp",EDGE,"E56"),sQuery(id+"F35.wireOp",EDGE,"E59"),sQuery(id+"F35.wireOp",EDGE,"E60"),sQuery(id+"F35.wireOp",EDGE,"E61"),sQuery(id+"F35.wireOp",EDGE,"E62")])],"isStart":true})]});}
            var sketch = newSketch(context, id + "F40", { "sketchPlane" : qUnion([Q0])});
            skLineSegment(sketch, "E64", {"start": v(-303.21, -6.99) * mm, "end": v(-292.1, -6.99) * mm});
            skLineSegment(sketch, "E65", {"start": v(-292.1, -6.99) * mm, "end": v(-298.45, -6.99) * mm});
            skLineSegment(sketch, "E66", {"start": v(-298.45, -6.99) * mm, "end": v(-295.28, -6.99) * mm});
            skLineSegment(sketch, "E67", {"start": v(-295.28, -6.99) * mm, "end": v(-298.45, -6.99) * mm});
            skLineSegment(sketch, "E68", {"start": v(-298.45, -6.99) * mm, "end": v(-303.21, -6.99) * mm});
            skLineSegment(sketch, "E69", {"start": v(-303.21, -6.98) * mm, "end": v(-300.83, -6.98) * mm});
            skLineSegment(sketch, "E70", {"start": v(-300.83, -6.99) * mm, "end": v(-302.02, -6.99) * mm});
            skArc(sketch, "E71", {"start": v(-302.02, -6.99) * mm, "mid": v(-301.92, -12.37) * mm, "end": v(-298.94, -16.86) * mm});
            skArc(sketch, "E72", {"start": v(-300.83, -6.99) * mm, "mid": v(-300.52, -12.04) * mm, "end": v(-298.94, -16.86) * mm});
            skLineSegment(sketch, "E73", {"start": v(-302.02, -6.98) * mm, "end": v(-300.83, -6.98) * mm});
            skSolve(sketch);
        }
        {
            var Q0;
            Q0=qSketchRegion(id+"F40",true);
            extrude(context, id + "F41", {"entities" : qUnion([Q0]), "operationType" : NewBodyOperationType.ADD, "depth" : -13.97 * mm, "hasSecondDirection" : true, "secondDirectionOppositeDirection" : true, "secondDirectionDepth" : 12.7 * mm});
        }
        {
            var Q0;
            Q0=makeQuery(id+"F41.opExtrude","CAP_FACE",FACE,{"disambiguationData":[OSD([sQuery(id+"F40.wireOp",EDGE,"E71"),sQuery(id+"F40.wireOp",EDGE,"E72"),sQuery(id+"F40.wireOp",EDGE,"E73")])],"isStart":true});
            extrude(context, id + "F42", {"entities" : qUnion([Q0]), "operationType" : NewBodyOperationType.ADD, "depth" : 12.7 * mm});
        }
        {
            var Q0;
            Q0=makeQuery(id+"F20.opExtrude","CAP_FACE",FACE,{"disambiguationData":[OSD([sQuery(id+"F19.wireOp",EDGE,"E38")])],"isStart":false});
            var sketch = newSketch(context, id + "F43", { "sketchPlane" : qUnion([Q0])});
            skCircle(sketch, "E74", {"center": v(0, 22.86) * mm, "radius": 6.99 * mm});
            skSolve(sketch);
        }
        {
            var Q0;
            Q0=qSketchRegion(id+"F43",true);
            extrude(context, id + "F44", {"entities" : qUnion([Q0]), "operationType" : NewBodyOperationType.REMOVE, "oppositeDirection" : true, "depth" : 177.8 * mm});
        }
        {
            var Q0;
            {var subQ0=sQuery(id+"F6.wireOp",EDGE,"E3.right");var subQ1=sQuery(id+"F6.wireOp",EDGE,"E3.bottom");var subQ4=sQuery(id+"F12.wireOp",EDGE,"E19");var subQ7=sQuery(id+"F10.wireOp",EDGE,"E7");Q0=makeQuery(id+"F13.boolean.opBoolean","SPLIT",EDGE,{"disambiguationData":[TD([makeQuery(id+"F13.opExtrude","SWEPT_FACE",FACE,{"disambiguationData":[OSD([subQ4])]})])],"derivedFrom":makeQuery(id+"F11.boolean.opBoolean","SPLIT",EDGE,{"disambiguationData":[TD([makeQuery(id+"F11.opExtrude","SWEPT_FACE",FACE,{"disambiguationData":[OSD([subQ7])]})])],"derivedFrom":makeQuery(id+"F7.opExtrude","SWEPT_EDGE",EDGE,{"disambiguationData":[OSD([subQ1,subQ0])]})})});}
            var Q1;
            {var subQ0=sQuery(id+"F6.wireOp",EDGE,"E3.left");var subQ3=sQuery(id+"F6.wireOp",EDGE,"E3.bottom");var subQ6=sQuery(id+"F10.wireOp",EDGE,"E7");var subQ9=sQuery(id+"F12.wireOp",EDGE,"E19");Q1=makeQuery(id+"F13.boolean.opBoolean","SPLIT",EDGE,{"disambiguationData":[TD([makeQuery(id+"F13.opExtrude","SWEPT_FACE",FACE,{"disambiguationData":[OSD([subQ9])]})])],"derivedFrom":makeQuery(id+"F11.boolean.opBoolean","SPLIT",EDGE,{"disambiguationData":[TD([makeQuery(id+"F11.opExtrude","SWEPT_FACE",FACE,{"disambiguationData":[OSD([subQ6])]})])],"derivedFrom":makeQuery(id+"F7.opExtrude","SWEPT_EDGE",EDGE,{"disambiguationData":[OSD([subQ3,subQ0])]})})});}
            var Q2;
            {var subQ0=sQuery(id+"F6.wireOp",EDGE,"E3.right");var subQ2=sQuery(id+"F17.wireOp",EDGE,"E36");var subQ3=sQuery(id+"F6.wireOp",EDGE,"E3.top");Q2=makeQuery(id+"F18.boolean.opBoolean","SPLIT",EDGE,{"disambiguationData":[TD([makeQuery(id+"F18.opExtrude","SWEPT_FACE",FACE,{"disambiguationData":[OSD([subQ2])]})])],"derivedFrom":makeQuery(id+"F7.opExtrude","SWEPT_EDGE",EDGE,{"disambiguationData":[OSD([subQ3,subQ0])]})});}
            var Q3;
            {var subQ0=sQuery(id+"F6.wireOp",EDGE,"E3.left");var subQ1=sQuery(id+"F6.wireOp",EDGE,"E3.top");var subQ4=sQuery(id+"F17.wireOp",EDGE,"E36");Q3=makeQuery(id+"F18.boolean.opBoolean","SPLIT",EDGE,{"disambiguationData":[TD([makeQuery(id+"F18.opExtrude","SWEPT_FACE",FACE,{"disambiguationData":[OSD([subQ4])]})])],"derivedFrom":makeQuery(id+"F7.opExtrude","SWEPT_EDGE",EDGE,{"disambiguationData":[OSD([subQ1,subQ0])]})});}
            fillet(context, id + "F45", {"entities" : qUnion([Q0, Q1, Q2, Q3]), "radius" : 7 * mm, "tangentPropagation" : true, "allowEdgeOverflow" : false});
        }
        {
            var Q0;
            {var subQ0=sQuery(id+"F6.wireOp",EDGE,"E3.left");var subQ1=sQuery(id+"F6.wireOp",EDGE,"E3.top");var subQ2=sQuery(id+"F6.wireOp",EDGE,"E3.bottom");Q0=makeQuery(id+"F42.boolean.opBoolean","MERGE",FACE,{"derivedFrom":[makeQuery(id+"F36.boolean.opBoolean","MERGE",FACE,{"derivedFrom":[makeQuery(id+"F18.boolean.opBoolean","MERGE",FACE,{"derivedFrom":[makeQuery(id+"F16.boolean.opBoolean","MERGE",FACE,{"derivedFrom":[makeQuery(id+"F13.boolean.opBoolean","MERGE",FACE,{"derivedFrom":[makeQuery(id+"F11.boolean.opBoolean","MERGE",FACE,{"derivedFrom":[makeQuery(id+"F9.boolean.opBoolean","MERGE",FACE,{"derivedFrom":[makeQuery(id+"F7.opExtrude","SWEPT_FACE",FACE,{"disambiguationData":[OSD([subQ0])]}),makeQuery(id+"F9.opExtrude","CAP_FACE",FACE,{"disambiguationData":[OSD([subQ2,sQuery(id+"F6.wireOp",EDGE,"E3.right"),sQuery(id+"F8.wireOp",EDGE,"E4"),sQuery(id+"F8.wireOp",EDGE,"E5"),sQuery(id+"F8.wireOp",EDGE,"E6")])],"isStart":false})]}),makeQuery(id+"F11.opExtrude","CAP_FACE",FACE,{"disambiguationData":[OSD([sQuery(id+"F10.wireOp",EDGE,"E7"),sQuery(id+"F10.wireOp",EDGE,"E8"),sQuery(id+"F10.wireOp",EDGE,"E9"),sQuery(id+"F10.wireOp",EDGE,"E10")])],"isStart":false})]}),makeQuery(id+"F13.opExtrude","CAP_FACE",FACE,{"disambiguationData":[OSD([sQuery(id+"F12.wireOp",EDGE,"E12"),sQuery(id+"F12.wireOp",EDGE,"E13"),sQuery(id+"F12.wireOp",EDGE,"E14"),sQuery(id+"F12.wireOp",EDGE,"E15"),sQuery(id+"F12.wireOp",EDGE,"E16"),sQuery(id+"F12.wireOp",EDGE,"E17"),sQuery(id+"F12.wireOp",EDGE,"E18"),sQuery(id+"F12.wireOp",EDGE,"E19"),sQuery(id+"F12.wireOp",EDGE,"E20")])],"isStart":true})]}),makeQuery(id+"F16.opExtrude","CAP_FACE",FACE,{"disambiguationData":[OSD([subQ2,subQ0,sQuery(id+"F15.wireOp",EDGE,"E27"),sQuery(id+"F15.wireOp",EDGE,"E28"),sQuery(id+"F15.wireOp",EDGE,"E29")])],"isStart":true})]}),makeQuery(id+"F18.opExtrude","CAP_FACE",FACE,{"disambiguationData":[OSD([subQ1,subQ0,sQuery(id+"F17.wireOp",EDGE,"E30"),sQuery(id+"F17.wireOp",EDGE,"E31"),sQuery(id+"F17.wireOp",EDGE,"E32")])],"isStart":true}),makeQuery(id+"F18.opExtrude","CAP_FACE",FACE,{"disambiguationData":[OSD([subQ1,subQ0,sQuery(id+"F17.wireOp",EDGE,"E34"),sQuery(id+"F17.wireOp",EDGE,"E35"),sQuery(id+"F17.wireOp",EDGE,"E36")])],"isStart":true})]}),makeQuery(id+"F36.opExtrude","CAP_FACE",FACE,{"disambiguationData":[OSD([sQuery(id+"F35.wireOp",EDGE,"E56"),sQuery(id+"F35.wireOp",EDGE,"E59"),sQuery(id+"F35.wireOp",EDGE,"E60"),sQuery(id+"F35.wireOp",EDGE,"E61"),sQuery(id+"F35.wireOp",EDGE,"E62")])],"isStart":true})]}),makeQuery(id+"F42.opExtrude","CAP_FACE",FACE,{"disambiguationData":[OSD([sQuery(id+"F40.wireOp",EDGE,"E71"),sQuery(id+"F40.wireOp",EDGE,"E72"),sQuery(id+"F40.wireOp",EDGE,"E73")])],"isStart":false})]});}
            var sketch = newSketch(context, id + "F46", { "sketchPlane" : qUnion([Q0])});
            skCircle(sketch, "E75", {"center": v(-247.4, -0.32) * mm, "radius": 2.16 * mm});
            skSolve(sketch);
        }
        {
            var Q0;
            Q0=qSketchRegion(id+"F46",true);
            extrude(context, id + "F47", {"entities" : qUnion([Q0]), "operationType" : NewBodyOperationType.ADD, "depth" : 6.35 * mm});
        }
        {
            var Q0;
            Q0=makeQuery(id+"F7.opExtrude","CAP_FACE",FACE,{"disambiguationData":[OSD([sQuery(id+"F6.wireOp",EDGE,"E3.bottom"),sQuery(id+"F6.wireOp",EDGE,"E3.top"),sQuery(id+"F6.wireOp",EDGE,"E3.left"),sQuery(id+"F6.wireOp",EDGE,"E3.right")])],"isStart":true});
            var sketch = newSketch(context, id + "F48", { "sketchPlane" : qUnion([Q0])});
            skCircle(sketch, "E76", {"center": v(0, 0) * mm, "radius": 3.18 * mm});
            skCircle(sketch, "E77", {"center": v(0, 0) * mm, "radius": 5.72 * mm});
            skSolve(sketch);
        }
        {
            var Q0;
            Q0=qSketchRegion(id+"F48",true);
            extrude(context, id + "F49", {"entities" : qUnion([Q0]), "operationType" : NewBodyOperationType.REMOVE, "oppositeDirection" : true, "depth" : 50.8 * mm});
        }
        {
            var Q0;
            {var subQ0=sQuery(id+"F6.wireOp",EDGE,"E3.left");var subQ1=sQuery(id+"F6.wireOp",EDGE,"E3.top");var subQ2=sQuery(id+"F6.wireOp",EDGE,"E3.bottom");Q0=makeQuery(id+"F42.boolean.opBoolean","MERGE",FACE,{"derivedFrom":[makeQuery(id+"F36.boolean.opBoolean","MERGE",FACE,{"derivedFrom":[makeQuery(id+"F18.boolean.opBoolean","MERGE",FACE,{"derivedFrom":[makeQuery(id+"F16.boolean.opBoolean","MERGE",FACE,{"derivedFrom":[makeQuery(id+"F13.boolean.opBoolean","MERGE",FACE,{"derivedFrom":[makeQuery(id+"F11.boolean.opBoolean","MERGE",FACE,{"derivedFrom":[makeQuery(id+"F9.boolean.opBoolean","MERGE",FACE,{"derivedFrom":[makeQuery(id+"F7.opExtrude","SWEPT_FACE",FACE,{"disambiguationData":[OSD([subQ0])]}),makeQuery(id+"F9.opExtrude","CAP_FACE",FACE,{"disambiguationData":[OSD([subQ2,sQuery(id+"F6.wireOp",EDGE,"E3.right"),sQuery(id+"F8.wireOp",EDGE,"E4"),sQuery(id+"F8.wireOp",EDGE,"E5"),sQuery(id+"F8.wireOp",EDGE,"E6")])],"isStart":false})]}),makeQuery(id+"F11.opExtrude","CAP_FACE",FACE,{"disambiguationData":[OSD([sQuery(id+"F10.wireOp",EDGE,"E7"),sQuery(id+"F10.wireOp",EDGE,"E8"),sQuery(id+"F10.wireOp",EDGE,"E9"),sQuery(id+"F10.wireOp",EDGE,"E10")])],"isStart":false})]}),makeQuery(id+"F13.opExtrude","CAP_FACE",FACE,{"disambiguationData":[OSD([sQuery(id+"F12.wireOp",EDGE,"E12"),sQuery(id+"F12.wireOp",EDGE,"E13"),sQuery(id+"F12.wireOp",EDGE,"E14"),sQuery(id+"F12.wireOp",EDGE,"E15"),sQuery(id+"F12.wireOp",EDGE,"E16"),sQuery(id+"F12.wireOp",EDGE,"E17"),sQuery(id+"F12.wireOp",EDGE,"E18"),sQuery(id+"F12.wireOp",EDGE,"E19"),sQuery(id+"F12.wireOp",EDGE,"E20")])],"isStart":true})]}),makeQuery(id+"F16.opExtrude","CAP_FACE",FACE,{"disambiguationData":[OSD([subQ2,subQ0,sQuery(id+"F15.wireOp",EDGE,"E27"),sQuery(id+"F15.wireOp",EDGE,"E28"),sQuery(id+"F15.wireOp",EDGE,"E29")])],"isStart":true})]}),makeQuery(id+"F18.opExtrude","CAP_FACE",FACE,{"disambiguationData":[OSD([subQ1,subQ0,sQuery(id+"F17.wireOp",EDGE,"E30"),sQuery(id+"F17.wireOp",EDGE,"E31"),sQuery(id+"F17.wireOp",EDGE,"E32")])],"isStart":true}),makeQuery(id+"F18.opExtrude","CAP_FACE",FACE,{"disambiguationData":[OSD([subQ1,subQ0,sQuery(id+"F17.wireOp",EDGE,"E34"),sQuery(id+"F17.wireOp",EDGE,"E35"),sQuery(id+"F17.wireOp",EDGE,"E36")])],"isStart":true})]}),makeQuery(id+"F36.opExtrude","CAP_FACE",FACE,{"disambiguationData":[OSD([sQuery(id+"F35.wireOp",EDGE,"E56"),sQuery(id+"F35.wireOp",EDGE,"E59"),sQuery(id+"F35.wireOp",EDGE,"E60"),sQuery(id+"F35.wireOp",EDGE,"E61"),sQuery(id+"F35.wireOp",EDGE,"E62")])],"isStart":true})]}),makeQuery(id+"F42.opExtrude","CAP_FACE",FACE,{"disambiguationData":[OSD([sQuery(id+"F40.wireOp",EDGE,"E71"),sQuery(id+"F40.wireOp",EDGE,"E72"),sQuery(id+"F40.wireOp",EDGE,"E73")])],"isStart":false})]});}
            var sketch = newSketch(context, id + "F50", { "sketchPlane" : qUnion([Q0])});
            skLineSegment(sketch, "E78", {"start": v(-234.95, 0) * mm, "end": v(-190.5, 0) * mm});
            skLineSegment(sketch, "E79", {"start": v(-234.95, 0) * mm, "end": v(-212.72, 0) * mm});
            skLineSegment(sketch, "E80", {"start": v(-212.72, 0) * mm, "end": v(-190.5, 0) * mm});
            skLineSegment(sketch, "E81", {"start": v(-190.5, 0) * mm, "end": v(-201.61, 0) * mm});
            skLineSegment(sketch, "E82", {"start": v(-201.61, 0) * mm, "end": v(-212.72, 0) * mm});
            skLineSegment(sketch, "E83", {"start": v(-212.72, 0) * mm, "end": v(-223.84, 0) * mm});
            skLineSegment(sketch, "E84", {"start": v(-223.84, 0) * mm, "end": v(-234.95, 0) * mm});
            skLineSegment(sketch, "E85", {"start": v(-234.95, 0) * mm, "end": v(-229.4, 0) * mm});
            skLineSegment(sketch, "E86", {"start": v(-229.4, 0) * mm, "end": v(-223.84, 0) * mm});
            skLineSegment(sketch, "E87", {"start": v(-223.84, 0) * mm, "end": v(-218.28, 0) * mm});
            skLineSegment(sketch, "E88", {"start": v(-218.28, 0) * mm, "end": v(-212.72, 0) * mm});
            skLineSegment(sketch, "E89", {"start": v(-212.72, 0) * mm, "end": v(-207.17, 0) * mm});
            skLineSegment(sketch, "E90", {"start": v(-207.17, 0) * mm, "end": v(-201.61, 0) * mm});
            skLineSegment(sketch, "E91", {"start": v(-201.61, 0) * mm, "end": v(-196.06, 0) * mm});
            skCircle(sketch, "E92", {"center": v(-229.4, 0) * mm, "radius": 1.27 * mm});
            skCircle(sketch, "E93", {"center": v(-223.84, 0) * mm, "radius": 1.27 * mm});
            skCircle(sketch, "E94", {"center": v(-218.28, 0) * mm, "radius": 1.27 * mm});
            skCircle(sketch, "E95", {"center": v(-212.72, 0) * mm, "radius": 1.27 * mm});
            skCircle(sketch, "E96", {"center": v(-207.17, 0) * mm, "radius": 1.27 * mm});
            skCircle(sketch, "E97", {"center": v(-201.61, 0) * mm, "radius": 1.27 * mm});
            skCircle(sketch, "E98", {"center": v(-196.06, 0) * mm, "radius": 1.27 * mm});
            skSolve(sketch);
        }
        {
            var Q0;
            Q0=qSketchRegion(id+"F50",true);
            extrude(context, id + "F51", {"entities" : qUnion([Q0]), "operationType" : NewBodyOperationType.REMOVE, "oppositeDirection" : true, "depth" : 2.54 * mm});
        }
        {
            var Q0;
            {var subQ0=sQuery(id+"F6.wireOp",EDGE,"E3.left");var subQ1=sQuery(id+"F6.wireOp",EDGE,"E3.top");var subQ2=sQuery(id+"F6.wireOp",EDGE,"E3.bottom");var subQ3=sQuery(id+"F6.wireOp",EDGE,"E3.right");Q0=makeQuery(id+"F41.boolean.opBoolean","MERGE",FACE,{"derivedFrom":[makeQuery(id+"F36.boolean.opBoolean","MERGE",FACE,{"derivedFrom":[makeQuery(id+"F18.boolean.opBoolean","MERGE",FACE,{"derivedFrom":[makeQuery(id+"F16.boolean.opBoolean","MERGE",FACE,{"derivedFrom":[makeQuery(id+"F13.boolean.opBoolean","MERGE",FACE,{"derivedFrom":[makeQuery(id+"F11.boolean.opBoolean","MERGE",FACE,{"derivedFrom":[makeQuery(id+"F9.boolean.opBoolean","MERGE",FACE,{"derivedFrom":[makeQuery(id+"F7.opExtrude","SWEPT_FACE",FACE,{"disambiguationData":[OSD([subQ3])]}),makeQuery(id+"F9.opExtrude","CAP_FACE",FACE,{"disambiguationData":[OSD([subQ2,subQ3,sQuery(id+"F8.wireOp",EDGE,"E4"),sQuery(id+"F8.wireOp",EDGE,"E5"),sQuery(id+"F8.wireOp",EDGE,"E6")])],"isStart":true})]}),makeQuery(id+"F11.opExtrude","CAP_FACE",FACE,{"disambiguationData":[OSD([sQuery(id+"F10.wireOp",EDGE,"E7"),sQuery(id+"F10.wireOp",EDGE,"E8"),sQuery(id+"F10.wireOp",EDGE,"E9"),sQuery(id+"F10.wireOp",EDGE,"E10")])],"isStart":true})]}),makeQuery(id+"F13.opExtrude","CAP_FACE",FACE,{"disambiguationData":[OSD([sQuery(id+"F12.wireOp",EDGE,"E12"),sQuery(id+"F12.wireOp",EDGE,"E13"),sQuery(id+"F12.wireOp",EDGE,"E14"),sQuery(id+"F12.wireOp",EDGE,"E15"),sQuery(id+"F12.wireOp",EDGE,"E16"),sQuery(id+"F12.wireOp",EDGE,"E17"),sQuery(id+"F12.wireOp",EDGE,"E18"),sQuery(id+"F12.wireOp",EDGE,"E19"),sQuery(id+"F12.wireOp",EDGE,"E20")])],"isStart":false})]}),makeQuery(id+"F16.opExtrude","CAP_FACE",FACE,{"disambiguationData":[OSD([subQ2,subQ0,sQuery(id+"F15.wireOp",EDGE,"E27"),sQuery(id+"F15.wireOp",EDGE,"E28"),sQuery(id+"F15.wireOp",EDGE,"E29")])],"isStart":false})]}),makeQuery(id+"F18.opExtrude","CAP_FACE",FACE,{"disambiguationData":[OSD([subQ1,subQ0,sQuery(id+"F17.wireOp",EDGE,"E30"),sQuery(id+"F17.wireOp",EDGE,"E31"),sQuery(id+"F17.wireOp",EDGE,"E32")])],"isStart":false}),makeQuery(id+"F18.opExtrude","CAP_FACE",FACE,{"disambiguationData":[OSD([subQ1,subQ0,sQuery(id+"F17.wireOp",EDGE,"E34"),sQuery(id+"F17.wireOp",EDGE,"E35"),sQuery(id+"F17.wireOp",EDGE,"E36")])],"isStart":false})]}),makeQuery(id+"F36.opExtrude","CAP_FACE",FACE,{"disambiguationData":[OSD([sQuery(id+"F35.wireOp",EDGE,"E56"),sQuery(id+"F35.wireOp",EDGE,"E59"),sQuery(id+"F35.wireOp",EDGE,"E60"),sQuery(id+"F35.wireOp",EDGE,"E61"),sQuery(id+"F35.wireOp",EDGE,"E62")])],"isStart":false})]}),makeQuery(id+"F41.opExtrude","CAP_FACE",FACE,{"disambiguationData":[OSD([sQuery(id+"F40.wireOp",EDGE,"E71"),sQuery(id+"F40.wireOp",EDGE,"E72"),sQuery(id+"F40.wireOp",EDGE,"E73")])],"isStart":false})]});}
            var sketch = newSketch(context, id + "F52", { "sketchPlane" : qUnion([Q0])});
            skLineSegment(sketch, "E99", {"start": v(234.95, 0) * mm, "end": v(190.5, 0) * mm});
            skLineSegment(sketch, "E100", {"start": v(234.95, 0) * mm, "end": v(212.72, 0) * mm});
            skLineSegment(sketch, "E101", {"start": v(212.72, 0) * mm, "end": v(223.84, 0) * mm});
            skLineSegment(sketch, "E102", {"start": v(223.84, 0) * mm, "end": v(212.72, 0) * mm});
            skLineSegment(sketch, "E103", {"start": v(212.72, 0) * mm, "end": v(190.5, 0) * mm});
            skLineSegment(sketch, "E104", {"start": v(190.5, 0) * mm, "end": v(201.61, 0) * mm});
            skLineSegment(sketch, "E105", {"start": v(201.61, 0) * mm, "end": v(212.72, 0) * mm});
            skLineSegment(sketch, "E106", {"start": v(234.95, 0) * mm, "end": v(223.84, 0) * mm});
            skLineSegment(sketch, "E107", {"start": v(234.95, 0) * mm, "end": v(229.4, 0) * mm});
            skLineSegment(sketch, "E108", {"start": v(229.4, 0) * mm, "end": v(223.84, 0) * mm});
            skLineSegment(sketch, "E109", {"start": v(223.84, 0) * mm, "end": v(218.28, 0) * mm});
            skLineSegment(sketch, "E110", {"start": v(218.28, 0) * mm, "end": v(212.72, 0) * mm});
            skLineSegment(sketch, "E111", {"start": v(212.72, 0) * mm, "end": v(207.17, 0) * mm});
            skLineSegment(sketch, "E112", {"start": v(207.17, 0) * mm, "end": v(201.61, 0) * mm});
            skLineSegment(sketch, "E113", {"start": v(201.61, 0) * mm, "end": v(196.06, 0) * mm});
            skCircle(sketch, "E114", {"center": v(229.4, 0) * mm, "radius": 1.27 * mm});
            skCircle(sketch, "E115", {"center": v(223.84, 0) * mm, "radius": 1.27 * mm});
            skCircle(sketch, "E116", {"center": v(218.28, 0) * mm, "radius": 1.27 * mm});
            skCircle(sketch, "E117", {"center": v(212.72, 0) * mm, "radius": 1.27 * mm});
            skCircle(sketch, "E118", {"center": v(207.17, 0) * mm, "radius": 1.27 * mm});
            skCircle(sketch, "E119", {"center": v(201.61, 0) * mm, "radius": 1.27 * mm});
            skCircle(sketch, "E120", {"center": v(196.06, 0) * mm, "radius": 1.27 * mm});
            skSolve(sketch);
        }
        {
            var Q0;
            Q0=qSketchRegion(id+"F52",true);
            extrude(context, id + "F53", {"entities" : qUnion([Q0]), "operationType" : NewBodyOperationType.REMOVE, "oppositeDirection" : true, "depth" : 2.54 * mm});
        }
        {
            var Q0;
            Q0=makeQuery(id+"F22.boolean.opBoolean","COPY",FACE,{"derivedFrom":makeQuery(id+"F22.opExtrude","CAP_FACE",FACE,{"disambiguationData":[OSD([sQuery(id+"F21.wireOp",EDGE,"E39"),sQuery(id+"F21.wireOp",EDGE,"E43"),sQuery(id+"F21.wireOp",EDGE,"E44"),sQuery(id+"F21.wireOp",EDGE,"E45")])],"isStart":false})});
            var sketch = newSketch(context, id + "F54", { "sketchPlane" : qUnion([Q0])});
            skLineSegment(sketch, "E121", {"start": v(-3.5, -283.21) * mm, "end": v(-3.5, -250.2) * mm});
            skLineSegment(sketch, "E122", {"start": v(3.5, -283.21) * mm, "end": v(3.5, -250.2) * mm});
            skLineSegment(sketch, "E123", {"start": v(-3.5, -283.21) * mm, "end": v(3.5, -283.21) * mm});
            skLineSegment(sketch, "E124", {"start": v(-3.5, -250.2) * mm, "end": v(3.5, -250.2) * mm});
            skSolve(sketch);
        }
        {
            var Q0;
            Q0=qSketchRegion(id+"F54",true);
            extrude(context, id + "F55", {"entities" : qUnion([Q0]), "operationType" : NewBodyOperationType.REMOVE, "oppositeDirection" : true, "depth" : 10.16 * mm});
        }
        {
            var Q0;
            Q0=makeQuery(id+"F1.opExtrude","SWEPT_EDGE",EDGE,{"disambiguationData":[OSD([sQuery(id+"F0.wireOp",EDGE,"E0.top"),sQuery(id+"F0.wireOp",EDGE,"E0.right")])]});
            var Q1;
            Q1=makeQuery(id+"F1.opExtrude","SWEPT_EDGE",EDGE,{"disambiguationData":[OSD([sQuery(id+"F0.wireOp",EDGE,"E0.bottom"),sQuery(id+"F0.wireOp",EDGE,"E0.right")])]});
            var Q2;
            Q2=makeQuery(id+"F1.opExtrude","SWEPT_EDGE",EDGE,{"disambiguationData":[OSD([sQuery(id+"F0.wireOp",EDGE,"E0.bottom"),sQuery(id+"F0.wireOp",EDGE,"E0.left")])]});
            var Q3;
            Q3=makeQuery(id+"F1.opExtrude","SWEPT_EDGE",EDGE,{"disambiguationData":[OSD([sQuery(id+"F0.wireOp",EDGE,"E0.top"),sQuery(id+"F0.wireOp",EDGE,"E0.left")])]});
            chamfer(context, id + "F56", {"entities" : qUnion([Q0, Q1, Q2, Q3]), "width" : 1.27 * mm, "tangentPropagation" : true});
        }
        {
            var Q0;
            Q0=makeQuery(id+"F11.opExtrude","CAP_EDGE",EDGE,{"disambiguationData":[OSD([sQuery(id+"F10.wireOp",EDGE,"E9")])],"isStart":false});
            var Q1;
            Q1=makeQuery(id+"F11.opExtrude","CAP_EDGE",EDGE,{"disambiguationData":[OSD([sQuery(id+"F10.wireOp",EDGE,"E9")])],"isStart":true});
            var Q2;
            Q2=makeQuery(id+"F9.opExtrude","CAP_EDGE",EDGE,{"disambiguationData":[OSD([sQuery(id+"F8.wireOp",EDGE,"E6")])],"isStart":false});
            var Q3;
            Q3=makeQuery(id+"F9.opExtrude","CAP_EDGE",EDGE,{"disambiguationData":[OSD([sQuery(id+"F8.wireOp",EDGE,"E6")])],"isStart":true});
            var Q4;
            {var subQ0=sQuery(id+"F8.wireOp",EDGE,"E6");var subQ1=sQuery(id+"F6.wireOp",EDGE,"E3.right");var subQ2=sQuery(id+"F6.wireOp",EDGE,"E3.bottom");Q4=makeQuery(id+"F11.boolean.opBoolean","SPLIT",EDGE,{"disambiguationData":[TD([makeQuery(id+"F9.opExtrude","SWEPT_FACE",FACE,{"disambiguationData":[OSD([subQ0])]})])],"derivedFrom":makeQuery(id+"F7.opExtrude","SWEPT_EDGE",EDGE,{"disambiguationData":[OSD([subQ2,subQ1])]})});}
            var Q5;
            {var subQ0=sQuery(id+"F8.wireOp",EDGE,"E6");var subQ1=sQuery(id+"F6.wireOp",EDGE,"E3.bottom");var subQ2=sQuery(id+"F6.wireOp",EDGE,"E3.left");Q5=makeQuery(id+"F11.boolean.opBoolean","SPLIT",EDGE,{"disambiguationData":[TD([makeQuery(id+"F9.opExtrude","SWEPT_FACE",FACE,{"disambiguationData":[OSD([subQ0])]})])],"derivedFrom":makeQuery(id+"F7.opExtrude","SWEPT_EDGE",EDGE,{"disambiguationData":[OSD([subQ1,subQ2])]})});}
            chamfer(context, id + "F57", {"entities" : qUnion([Q0, Q1, Q2, Q3, Q4, Q5]), "width" : 2.54 * mm, "tangentPropagation" : true});
        }
        {
            var Q0;
            {var subQ1=sQuery(id+"F4.wireOp",EDGE,"E2.right");Q0=makeQuery(id+"F5.boolean.opBoolean","SPLIT",FACE,{"disambiguationData":[TD([makeQuery(id+"F1.opExtrude","SWEPT_FACE",FACE,{"disambiguationData":[OSD([sQuery(id+"F0.wireOp",EDGE,"E0.bottom")])]})])],"derivedFrom":makeQuery(id+"F5.opExtrude","SWEPT_FACE",FACE,{"disambiguationData":[OSD([subQ1])]})});}
            var sketch = newSketch(context, id + "F58", { "sketchPlane" : qUnion([Q0])});
            skLineSegment(sketch, "E125", {"start": v(12.7, -12.7) * mm, "end": v(15.88, -12.7) * mm});
            skLineSegment(sketch, "E126", {"start": v(15.88, -12.7) * mm, "end": v(15.88, -6.35) * mm});
            skLineSegment(sketch, "E127", {"start": v(15.88, -6.35) * mm, "end": v(15.88, -9.53) * mm});
            skSolve(sketch);
        }
        {
            var Q0;
            Q0=sQuery(id+"F58.wireOp",VERTEX,"E127.end");
            var Q1;
            Q1=makeQuery(id+"F1.opExtrude","SWEPT_BODY",BODY,{"disambiguationData":[OSD([sQuery(id+"F0.wireOp",EDGE,"E0.bottom"),sQuery(id+"F0.wireOp",EDGE,"E0.top"),sQuery(id+"F0.wireOp",EDGE,"E0.left"),sQuery(id+"F0.wireOp",EDGE,"E0.right")])]});
            hole(context, id + "F59", {"style" : HoleStyle.SIMPLE, "endStyle" : HoleEndStyle.BLIND, "holeDiameter" : 3.8 * mm, "holeDepth" : 254 * mm, "tappedDepth" : 12.7 * mm, "tapClearance" : 3, "locations" : qUnion([Q0]), "scope" : qUnion([Q1])});
        }
        {
            var Q0;
            {var subQ0=sQuery(id+"F4.wireOp",EDGE,"E2.right");Q0=makeQuery(id+"F5.boolean.opBoolean","SPLIT",FACE,{"disambiguationData":[TD([makeQuery(id+"F1.opExtrude","SWEPT_FACE",FACE,{"disambiguationData":[OSD([sQuery(id+"F0.wireOp",EDGE,"E0.top")])]})])],"derivedFrom":makeQuery(id+"F5.opExtrude","SWEPT_FACE",FACE,{"disambiguationData":[OSD([subQ0])]})});}
            var sketch = newSketch(context, id + "F60", { "sketchPlane" : qUnion([Q0])});
            skLineSegment(sketch, "E128", {"start": v(12.7, 12.7) * mm, "end": v(15.88, 12.7) * mm});
            skLineSegment(sketch, "E129", {"start": v(15.88, 12.7) * mm, "end": v(15.88, 6.35) * mm});
            skLineSegment(sketch, "E130", {"start": v(15.88, 6.35) * mm, "end": v(15.88, 9.53) * mm});
            skSolve(sketch);
        }
        {
            var Q0;
            Q0=sQuery(id+"F60.wireOp",VERTEX,"E130.end");
            var Q1;
            Q1=makeQuery(id+"F1.opExtrude","SWEPT_BODY",BODY,{"disambiguationData":[OSD([sQuery(id+"F0.wireOp",EDGE,"E0.bottom"),sQuery(id+"F0.wireOp",EDGE,"E0.top"),sQuery(id+"F0.wireOp",EDGE,"E0.left"),sQuery(id+"F0.wireOp",EDGE,"E0.right")])]});
            hole(context, id + "F61", {"style" : HoleStyle.SIMPLE, "endStyle" : HoleEndStyle.BLIND, "holeDiameter" : 3.8 * mm, "holeDepth" : 254 * mm, "tappedDepth" : 12.7 * mm, "tapClearance" : 3, "locations" : qUnion([Q0]), "scope" : qUnion([Q1])});
        }
    });
